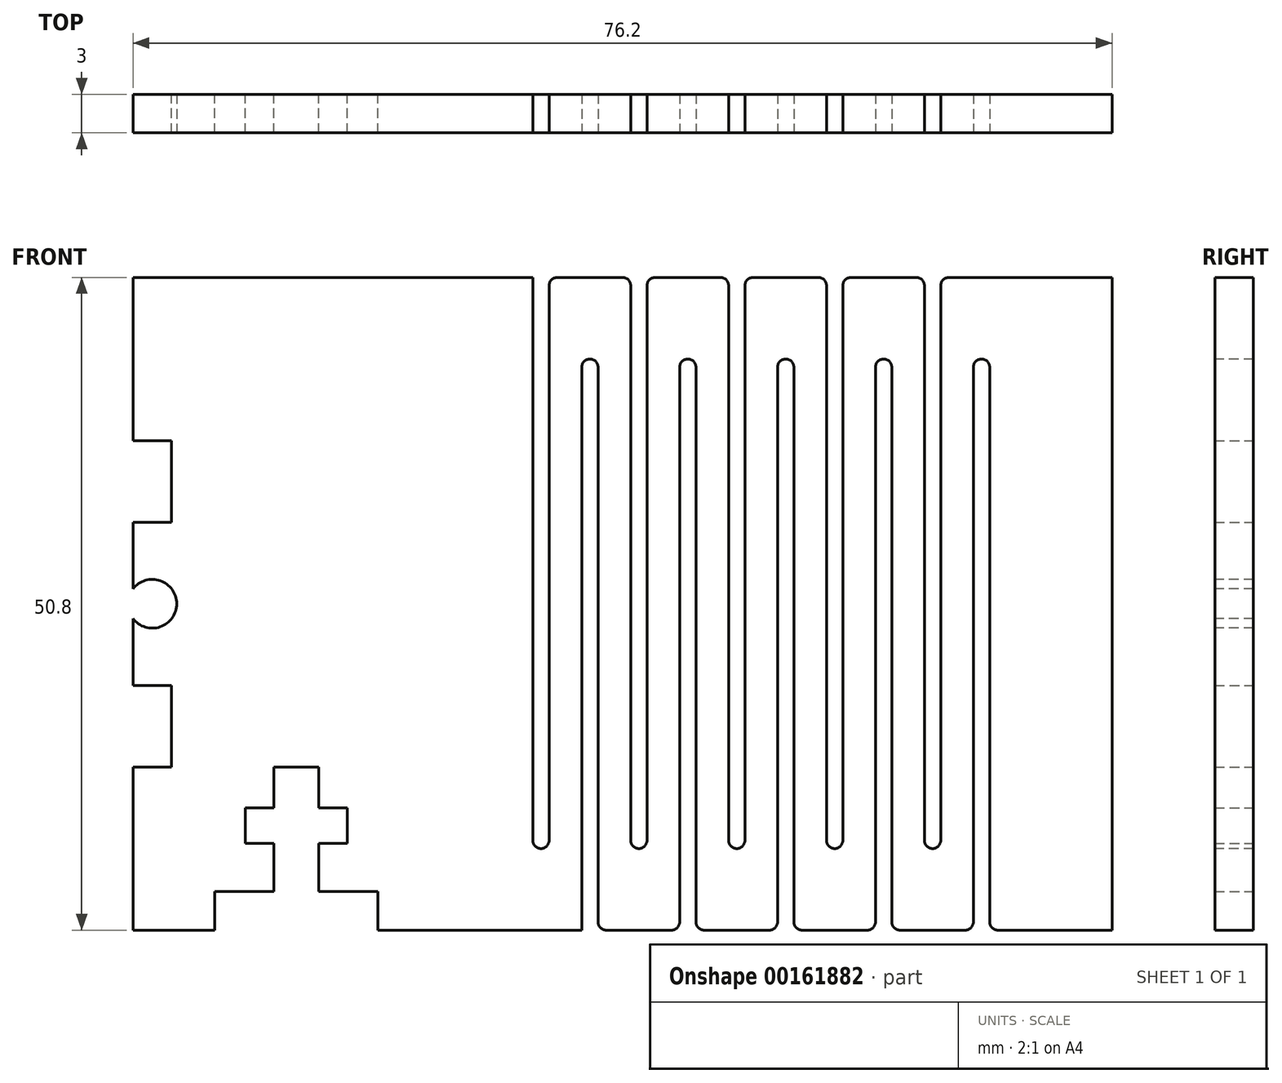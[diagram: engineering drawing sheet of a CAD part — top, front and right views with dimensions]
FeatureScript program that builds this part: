
annotation { "Feature Type Name" : "Feature", "Feature Type Description" : "" }
export const myFeature = defineFeature(function(context is Context, id is Id, definition is map)
    precondition{}
    {
        {
            var Q0;
            Q0=qCreatedBy(makeId("Front.planeOp"),FACE);
            var sketch = newSketch(context, id + "F0", { "sketchPlane" : qUnion([Q0])});
            skLineSegment(sketch, "E0.bottom", {"start": v(-38.1, 25.4) * mm, "end": v(38.1, 25.4) * mm});
            skLineSegment(sketch, "E0.top", {"start": v(-38.1, -25.4) * mm, "end": v(-31.75, -25.4) * mm});
            skLineSegment(sketch, "E0.left", {"start": v(-38.1, 25.4) * mm, "end": v(-38.1, 12.7) * mm});
            skLineSegment(sketch, "E0.right", {"start": v(38.1, 25.4) * mm, "end": v(38.1, -25.4) * mm});
            skPoint(sketch, "E0.middle", {"position": v(0, 0) * mm});
            skLineSegment(sketch, "E1", {"start": v(-31.75, -25.4) * mm, "end": v(-31.75, -22.4) * mm});
            skLineSegment(sketch, "E2", {"start": v(-31.75, -22.4) * mm, "end": v(-27.15, -22.4) * mm});
            skLineSegment(sketch, "E3", {"start": v(-23.65, -22.4) * mm, "end": v(-23.65, -18.64) * mm});
            skLineSegment(sketch, "E4", {"start": v(-29.36, -18.64) * mm, "end": v(-29.36, -15.88) * mm});
            skLineSegment(sketch, "E5", {"start": v(-23.65, -15.88) * mm, "end": v(-23.65, -12.7) * mm});
            skLineSegment(sketch, "E6", {"start": v(-27.15, -12.7) * mm, "end": v(-23.65, -12.7) * mm});
            skLineSegment(sketch, "E7", {"start": v(-27.15, -12.7) * mm, "end": v(-27.15, -15.88) * mm});
            skLineSegment(sketch, "E8", {"start": v(-27.15, -18.64) * mm, "end": v(-27.15, -22.4) * mm});
            skLineSegment(sketch, "E9", {"start": v(-19.05, -22.4) * mm, "end": v(-19.05, -25.4) * mm});
            skLineSegment(sketch, "E10", {"start": v(-25.4, -12.7) * mm, "end": v(-25.4, -25.4) * mm, "construction": true});
            skLineSegment(sketch, "E11", {"start": v(-29.36, -15.88) * mm, "end": v(-27.15, -15.88) * mm});
            skLineSegment(sketch, "E12", {"start": v(-29.36, -18.64) * mm, "end": v(-27.15, -18.64) * mm});
            skLineSegment(sketch, "E13", {"start": v(-23.65, -15.88) * mm, "end": v(-21.44, -15.88) * mm});
            skLineSegment(sketch, "E14", {"start": v(-21.44, -15.88) * mm, "end": v(-21.44, -18.64) * mm});
            skLineSegment(sketch, "E15", {"start": v(-21.44, -18.64) * mm, "end": v(-23.65, -18.64) * mm});
            skLineSegment(sketch, "E16.trimOffspring", {"start": v(-23.65, -22.4) * mm, "end": v(-19.05, -22.4) * mm});
            skLineSegment(sketch, "E17.trimOffspring", {"start": v(-19.05, -25.4) * mm, "end": v(38.1, -25.4) * mm});
            skLineSegment(sketch, "E18", {"start": v(-38.1, 6.35) * mm, "end": v(-35.1, 6.35) * mm});
            skLineSegment(sketch, "E19", {"start": v(-35.1, 6.35) * mm, "end": v(-35.1, 12.7) * mm});
            skLineSegment(sketch, "E20", {"start": v(-35.1, 12.7) * mm, "end": v(-38.1, 12.7) * mm});
            skLineSegment(sketch, "E21", {"start": v(-38.1, -6.35) * mm, "end": v(-35.1, -6.35) * mm});
            skLineSegment(sketch, "E22", {"start": v(-35.1, -6.35) * mm, "end": v(-35.1, -12.7) * mm});
            skLineSegment(sketch, "E23", {"start": v(-35.1, -12.7) * mm, "end": v(-38.1, -12.7) * mm});
            skLineSegment(sketch, "E24.trimOffspring", {"start": v(-38.1, 6.35) * mm, "end": v(-38.1, -6.35) * mm});
            skLineSegment(sketch, "E25.trimOffspring", {"start": v(-38.1, -12.7) * mm, "end": v(-38.1, -25.4) * mm});
            skSolve(sketch);
        }
        {
            var Q0;
            Q0 = qSketchRegion(id + "F0", true);
            extrude(context, id + "F1", {"entities" : qUnion([Q0]), "depth" : 3 * mm});
        }
        {
            var Q0;
            Q0=makeQuery(id+"F1.opExtrude","CAP_FACE",FACE,{"disambiguationData":[OSD([sQuery(id+"F0.wireOp",EDGE,"E0.bottom"),sQuery(id+"F0.wireOp",EDGE,"E0.top"),sQuery(id+"F0.wireOp",EDGE,"E0.left"),sQuery(id+"F0.wireOp",EDGE,"E0.right"),sQuery(id+"F0.wireOp",EDGE,"E1"),sQuery(id+"F0.wireOp",EDGE,"E2"),sQuery(id+"F0.wireOp",EDGE,"E3"),sQuery(id+"F0.wireOp",EDGE,"E4"),sQuery(id+"F0.wireOp",EDGE,"E5"),sQuery(id+"F0.wireOp",EDGE,"E6"),sQuery(id+"F0.wireOp",EDGE,"E7"),sQuery(id+"F0.wireOp",EDGE,"E8"),sQuery(id+"F0.wireOp",EDGE,"E9"),sQuery(id+"F0.wireOp",EDGE,"E11"),sQuery(id+"F0.wireOp",EDGE,"E12"),sQuery(id+"F0.wireOp",EDGE,"E13"),sQuery(id+"F0.wireOp",EDGE,"E14"),sQuery(id+"F0.wireOp",EDGE,"E15"),sQuery(id+"F0.wireOp",EDGE,"E16.trimOffspring"),sQuery(id+"F0.wireOp",EDGE,"E17.trimOffspring")])],"isStart":false});
            var sketch = newSketch(context, id + "F2", { "sketchPlane" : qUnion([Q0])});
            skLineSegment(sketch, "E26.0", {"start": v(-36.6, 6.35) * mm, "end": v(-36.6, -6.35) * mm, "construction": true});
            skPoint(sketch, "E27", {"position": v(-36.6, 0) * mm});
            skSolve(sketch);
        }
        {
            var Q0;
            Q0=sQuery(id+"F2.wireOp",VERTEX,"E27");
            var Q1;
            Q1=makeQuery(id+"F1.opExtrude","SWEPT_BODY",BODY,{"disambiguationData":[OSD([sQuery(id+"F0.wireOp",EDGE,"E0.bottom"),sQuery(id+"F0.wireOp",EDGE,"E0.top"),sQuery(id+"F0.wireOp",EDGE,"E0.left"),sQuery(id+"F0.wireOp",EDGE,"E0.right"),sQuery(id+"F0.wireOp",EDGE,"E1"),sQuery(id+"F0.wireOp",EDGE,"E2"),sQuery(id+"F0.wireOp",EDGE,"E3"),sQuery(id+"F0.wireOp",EDGE,"E4"),sQuery(id+"F0.wireOp",EDGE,"E5"),sQuery(id+"F0.wireOp",EDGE,"E6"),sQuery(id+"F0.wireOp",EDGE,"E7"),sQuery(id+"F0.wireOp",EDGE,"E8"),sQuery(id+"F0.wireOp",EDGE,"E9"),sQuery(id+"F0.wireOp",EDGE,"E11"),sQuery(id+"F0.wireOp",EDGE,"E12"),sQuery(id+"F0.wireOp",EDGE,"E13"),sQuery(id+"F0.wireOp",EDGE,"E14"),sQuery(id+"F0.wireOp",EDGE,"E15"),sQuery(id+"F0.wireOp",EDGE,"E16.trimOffspring"),sQuery(id+"F0.wireOp",EDGE,"E17.trimOffspring"),sQuery(id+"F0.wireOp",EDGE,"E18"),sQuery(id+"F0.wireOp",EDGE,"E19"),sQuery(id+"F0.wireOp",EDGE,"E20"),sQuery(id+"F0.wireOp",EDGE,"E21"),sQuery(id+"F0.wireOp",EDGE,"E22"),sQuery(id+"F0.wireOp",EDGE,"E23"),sQuery(id+"F0.wireOp",EDGE,"E24.trimOffspring"),sQuery(id+"F0.wireOp",EDGE,"E25.trimOffspring")])]});
            hole(context, id + "F3", {"style" : HoleStyle.SIMPLE, "endStyle" : HoleEndStyle.THROUGH, "standardTappedOrClearance" : lookupTablePath({ "standard" : "ANSI", "fit" : "Normal (ASME)", "size" : "#6", "type" : "Clearance" }), "standardBlindInLast" : lookupTablePath({ "fit" : "Free", "standard" : "ANSI", "size" : "#6", "type" : "Clearance" }), "holeDiameter" : 3.8 * mm, "locations" : qUnion([Q0]), "scope" : qUnion([Q1]), "isTappedThrough" : true});
        }
        {
            var Q0;
            Q0=makeQuery(id+"F1.opExtrude","CAP_FACE",FACE,{"disambiguationData":[OSD([sQuery(id+"F0.wireOp",EDGE,"E0.bottom"),sQuery(id+"F0.wireOp",EDGE,"E0.top"),sQuery(id+"F0.wireOp",EDGE,"E0.left"),sQuery(id+"F0.wireOp",EDGE,"E0.right"),sQuery(id+"F0.wireOp",EDGE,"E1"),sQuery(id+"F0.wireOp",EDGE,"E2"),sQuery(id+"F0.wireOp",EDGE,"E3"),sQuery(id+"F0.wireOp",EDGE,"E4"),sQuery(id+"F0.wireOp",EDGE,"E5"),sQuery(id+"F0.wireOp",EDGE,"E6"),sQuery(id+"F0.wireOp",EDGE,"E7"),sQuery(id+"F0.wireOp",EDGE,"E8"),sQuery(id+"F0.wireOp",EDGE,"E9"),sQuery(id+"F0.wireOp",EDGE,"E11"),sQuery(id+"F0.wireOp",EDGE,"E12"),sQuery(id+"F0.wireOp",EDGE,"E13"),sQuery(id+"F0.wireOp",EDGE,"E14"),sQuery(id+"F0.wireOp",EDGE,"E15"),sQuery(id+"F0.wireOp",EDGE,"E16.trimOffspring"),sQuery(id+"F0.wireOp",EDGE,"E17.trimOffspring"),sQuery(id+"F0.wireOp",EDGE,"E18"),sQuery(id+"F0.wireOp",EDGE,"E19"),sQuery(id+"F0.wireOp",EDGE,"E20"),sQuery(id+"F0.wireOp",EDGE,"E21"),sQuery(id+"F0.wireOp",EDGE,"E22"),sQuery(id+"F0.wireOp",EDGE,"E23"),sQuery(id+"F0.wireOp",EDGE,"E24.trimOffspring"),sQuery(id+"F0.wireOp",EDGE,"E25.trimOffspring")])],"isStart":false});
            var sketch = newSketch(context, id + "F4", { "sketchPlane" : qUnion([Q0])});
            skLineSegment(sketch, "E28", {"start": v(-12.7, 25.4) * mm, "end": v(-12.7, -25.4) * mm, "construction": true});
            skLineSegment(sketch, "E29.0", {"start": v(-6.35, 25.4) * mm, "end": v(-6.35, -19.05) * mm, "construction": true});
            skLineSegment(sketch, "E30.0", {"start": v(-6.98, 25.4) * mm, "end": v(-6.98, -19.05) * mm});
            skLineSegment(sketch, "E31.0", {"start": v(-5.71, 25.4) * mm, "end": v(-5.71, -19.05) * mm});
            skLineSegment(sketch, "E32.1.0.0", {"start": v(-3.17, 19.05) * mm, "end": v(-3.17, -25.4) * mm});
            skLineSegment(sketch, "E32.1.0.1", {"start": v(-2.54, 19.05) * mm, "end": v(-2.54, -25.4) * mm, "construction": true});
            skLineSegment(sketch, "E32.1.0.2", {"start": v(-1.9, 19.05) * mm, "end": v(-1.9, -25.4) * mm});
            skLineSegment(sketch, "E33.0", {"start": v(-3.17, 19.05) * mm, "end": v(-1.9, 19.05) * mm});
            skLineSegment(sketch, "E34.trimOffspring", {"start": v(-6.98, -19.05) * mm, "end": v(-5.71, -19.05) * mm});
            skLineSegment(sketch, "E35", {"start": v(-3.17, -25.4) * mm, "end": v(-1.9, -25.4) * mm});
            skLineSegment(sketch, "E36", {"start": v(-5.71, 25.4) * mm, "end": v(-6.98, 25.4) * mm});
            skLineSegment(sketch, "E37.1.0.0", {"start": v(5.72, 19.05) * mm, "end": v(5.72, -25.4) * mm});
            skLineSegment(sketch, "E37.1.0.1", {"start": v(1.27, 25.4) * mm, "end": v(1.27, -19.05) * mm, "construction": true});
            skLineSegment(sketch, "E37.1.0.2", {"start": v(4.45, 19.05) * mm, "end": v(4.45, -25.4) * mm});
            skLineSegment(sketch, "E37.1.0.3", {"start": v(0.64, 25.4) * mm, "end": v(0.64, -19.05) * mm});
            skLineSegment(sketch, "E37.1.0.4", {"start": v(1.9, 25.4) * mm, "end": v(1.9, -19.05) * mm});
            skLineSegment(sketch, "E37.1.0.5", {"start": v(5.08, 19.05) * mm, "end": v(5.08, -25.4) * mm, "construction": true});
            skLineSegment(sketch, "E37.1.0.6", {"start": v(0.64, -19.05) * mm, "end": v(1.9, -19.05) * mm});
            skLineSegment(sketch, "E37.1.0.7", {"start": v(4.45, -25.4) * mm, "end": v(5.72, -25.4) * mm});
            skLineSegment(sketch, "E37.1.0.8", {"start": v(1.9, 25.4) * mm, "end": v(0.64, 25.4) * mm});
            skLineSegment(sketch, "E37.1.0.9", {"start": v(4.45, 19.05) * mm, "end": v(5.72, 19.05) * mm});
            skLineSegment(sketch, "E37.2.0.0", {"start": v(13.34, 19.05) * mm, "end": v(13.34, -25.4) * mm});
            skLineSegment(sketch, "E37.2.0.1", {"start": v(8.9, 25.4) * mm, "end": v(8.9, -19.05) * mm, "construction": true});
            skLineSegment(sketch, "E37.2.0.2", {"start": v(12.07, 19.05) * mm, "end": v(12.07, -25.4) * mm});
            skLineSegment(sketch, "E37.2.0.3", {"start": v(8.26, 25.4) * mm, "end": v(8.26, -19.05) * mm});
            skLineSegment(sketch, "E37.2.0.4", {"start": v(9.53, 25.4) * mm, "end": v(9.53, -19.05) * mm});
            skLineSegment(sketch, "E37.2.0.5", {"start": v(12.7, 19.05) * mm, "end": v(12.7, -25.4) * mm, "construction": true});
            skLineSegment(sketch, "E37.2.0.6", {"start": v(8.26, -19.05) * mm, "end": v(9.53, -19.05) * mm});
            skLineSegment(sketch, "E37.2.0.7", {"start": v(12.07, -25.4) * mm, "end": v(13.34, -25.4) * mm});
            skLineSegment(sketch, "E37.2.0.8", {"start": v(9.53, 25.4) * mm, "end": v(8.26, 25.4) * mm});
            skLineSegment(sketch, "E37.2.0.9", {"start": v(12.07, 19.05) * mm, "end": v(13.34, 19.05) * mm});
            skLineSegment(sketch, "E37.3.0.0", {"start": v(20.96, 19.05) * mm, "end": v(20.96, -25.4) * mm});
            skLineSegment(sketch, "E37.3.0.1", {"start": v(16.51, 25.4) * mm, "end": v(16.51, -19.05) * mm, "construction": true});
            skLineSegment(sketch, "E37.3.0.2", {"start": v(19.69, 19.05) * mm, "end": v(19.69, -25.4) * mm});
            skLineSegment(sketch, "E37.3.0.3", {"start": v(15.88, 25.4) * mm, "end": v(15.88, -19.05) * mm});
            skLineSegment(sketch, "E37.3.0.4", {"start": v(17.15, 25.4) * mm, "end": v(17.15, -19.05) * mm});
            skLineSegment(sketch, "E37.3.0.5", {"start": v(20.32, 19.05) * mm, "end": v(20.32, -25.4) * mm, "construction": true});
            skLineSegment(sketch, "E37.3.0.6", {"start": v(15.88, -19.05) * mm, "end": v(17.15, -19.05) * mm});
            skLineSegment(sketch, "E37.3.0.7", {"start": v(19.69, -25.4) * mm, "end": v(20.96, -25.4) * mm});
            skLineSegment(sketch, "E37.3.0.8", {"start": v(17.15, 25.4) * mm, "end": v(15.88, 25.4) * mm});
            skLineSegment(sketch, "E37.3.0.9", {"start": v(19.69, 19.05) * mm, "end": v(20.96, 19.05) * mm});
            skLineSegment(sketch, "E37.4.0.0", {"start": v(28.58, 19.05) * mm, "end": v(28.58, -25.4) * mm});
            skLineSegment(sketch, "E37.4.0.1", {"start": v(24.13, 25.4) * mm, "end": v(24.13, -19.05) * mm, "construction": true});
            skLineSegment(sketch, "E37.4.0.2", {"start": v(27.3, 19.05) * mm, "end": v(27.3, -25.4) * mm});
            skLineSegment(sketch, "E37.4.0.3", {"start": v(23.5, 25.4) * mm, "end": v(23.5, -19.05) * mm});
            skLineSegment(sketch, "E37.4.0.4", {"start": v(24.77, 25.4) * mm, "end": v(24.77, -19.05) * mm});
            skLineSegment(sketch, "E37.4.0.5", {"start": v(27.94, 19.05) * mm, "end": v(27.94, -25.4) * mm, "construction": true});
            skLineSegment(sketch, "E37.4.0.6", {"start": v(23.5, -19.05) * mm, "end": v(24.77, -19.05) * mm});
            skLineSegment(sketch, "E37.4.0.7", {"start": v(27.3, -25.4) * mm, "end": v(28.58, -25.4) * mm});
            skLineSegment(sketch, "E37.4.0.8", {"start": v(24.77, 25.4) * mm, "end": v(23.5, 25.4) * mm});
            skLineSegment(sketch, "E37.4.0.9", {"start": v(27.3, 19.05) * mm, "end": v(28.58, 19.05) * mm});
            skLineSegment(sketch, "E37.direction1", {"start": v(-3.17, -25.4) * mm, "end": v(4.45, -25.4) * mm, "construction": true});
            skSolve(sketch);
        }
        {
            var Q0;
            Q0 = qSketchRegion(id + "F4", true);
            extrude(context, id + "F5", {"entities" : qUnion([Q0]), "operationType" : NewBodyOperationType.REMOVE, "endBound" : BoundingType.THROUGH_ALL, "oppositeDirection" : true, "depth" : 25.4 * mm});
        }
        {
            var Q0;
            Q0=makeQuery(id+"F5.boolean.opBoolean","COPY",EDGE,{"derivedFrom":makeQuery(id+"F5.opExtrude","SWEPT_EDGE",EDGE,{"disambiguationData":[OSD([sQuery(id+"F4.wireOp",EDGE,"E30.0"),sQuery(id+"F4.wireOp",EDGE,"E34.trimOffspring")])]})});
            var Q1;
            Q1=makeQuery(id+"F5.boolean.opBoolean","COPY",EDGE,{"derivedFrom":makeQuery(id+"F5.opExtrude","SWEPT_EDGE",EDGE,{"disambiguationData":[OSD([sQuery(id+"F4.wireOp",EDGE,"E31.0"),sQuery(id+"F4.wireOp",EDGE,"E34.trimOffspring")])]})});
            var Q2;
            Q2=makeQuery(id+"F5.boolean.opBoolean","COPY",EDGE,{"derivedFrom":makeQuery(id+"F5.opExtrude","SWEPT_EDGE",EDGE,{"disambiguationData":[OSD([sQuery(id+"F4.wireOp",EDGE,"E37.1.0.3"),sQuery(id+"F4.wireOp",EDGE,"E37.1.0.6")])]})});
            var Q3;
            Q3=makeQuery(id+"F5.boolean.opBoolean","COPY",EDGE,{"derivedFrom":makeQuery(id+"F5.opExtrude","SWEPT_EDGE",EDGE,{"disambiguationData":[OSD([sQuery(id+"F4.wireOp",EDGE,"E37.1.0.4"),sQuery(id+"F4.wireOp",EDGE,"E37.1.0.6")])]})});
            var Q4;
            Q4=makeQuery(id+"F5.boolean.opBoolean","COPY",EDGE,{"derivedFrom":makeQuery(id+"F5.opExtrude","SWEPT_EDGE",EDGE,{"disambiguationData":[OSD([sQuery(id+"F4.wireOp",EDGE,"E37.2.0.4"),sQuery(id+"F4.wireOp",EDGE,"E37.2.0.6")])]})});
            var Q5;
            Q5=makeQuery(id+"F5.boolean.opBoolean","COPY",EDGE,{"derivedFrom":makeQuery(id+"F5.opExtrude","SWEPT_EDGE",EDGE,{"disambiguationData":[OSD([sQuery(id+"F4.wireOp",EDGE,"E37.2.0.3"),sQuery(id+"F4.wireOp",EDGE,"E37.2.0.6")])]})});
            var Q6;
            Q6=makeQuery(id+"F5.boolean.opBoolean","COPY",EDGE,{"derivedFrom":makeQuery(id+"F5.opExtrude","SWEPT_EDGE",EDGE,{"disambiguationData":[OSD([sQuery(id+"F4.wireOp",EDGE,"E37.3.0.3"),sQuery(id+"F4.wireOp",EDGE,"E37.3.0.6")])]})});
            var Q7;
            Q7=makeQuery(id+"F5.boolean.opBoolean","COPY",EDGE,{"derivedFrom":makeQuery(id+"F5.opExtrude","SWEPT_EDGE",EDGE,{"disambiguationData":[OSD([sQuery(id+"F4.wireOp",EDGE,"E37.3.0.4"),sQuery(id+"F4.wireOp",EDGE,"E37.3.0.6")])]})});
            var Q8;
            Q8=makeQuery(id+"F5.boolean.opBoolean","COPY",EDGE,{"derivedFrom":makeQuery(id+"F5.opExtrude","SWEPT_EDGE",EDGE,{"disambiguationData":[OSD([sQuery(id+"F4.wireOp",EDGE,"E37.4.0.4"),sQuery(id+"F4.wireOp",EDGE,"E37.4.0.6")])]})});
            var Q9;
            Q9=makeQuery(id+"F5.boolean.opBoolean","COPY",EDGE,{"derivedFrom":makeQuery(id+"F5.opExtrude","SWEPT_EDGE",EDGE,{"disambiguationData":[OSD([sQuery(id+"F4.wireOp",EDGE,"E37.4.0.3"),sQuery(id+"F4.wireOp",EDGE,"E37.4.0.6")])]})});
            var Q10;
            Q10=makeQuery(id+"F5.boolean.opBoolean","COPY",EDGE,{"derivedFrom":makeQuery(id+"F5.opExtrude","SWEPT_EDGE",EDGE,{"disambiguationData":[OSD([sQuery(id+"F4.wireOp",EDGE,"E32.1.0.0"),sQuery(id+"F4.wireOp",EDGE,"E33.0")])]})});
            var Q11;
            Q11=makeQuery(id+"F5.boolean.opBoolean","COPY",EDGE,{"derivedFrom":makeQuery(id+"F5.opExtrude","SWEPT_EDGE",EDGE,{"disambiguationData":[OSD([sQuery(id+"F4.wireOp",EDGE,"E37.1.0.2"),sQuery(id+"F4.wireOp",EDGE,"E37.1.0.9")])]})});
            var Q12;
            Q12=makeQuery(id+"F5.boolean.opBoolean","COPY",EDGE,{"derivedFrom":makeQuery(id+"F5.opExtrude","SWEPT_EDGE",EDGE,{"disambiguationData":[OSD([sQuery(id+"F4.wireOp",EDGE,"E37.2.0.2"),sQuery(id+"F4.wireOp",EDGE,"E37.2.0.9")])]})});
            var Q13;
            Q13=makeQuery(id+"F5.boolean.opBoolean","COPY",EDGE,{"derivedFrom":makeQuery(id+"F5.opExtrude","SWEPT_EDGE",EDGE,{"disambiguationData":[OSD([sQuery(id+"F4.wireOp",EDGE,"E37.3.0.2"),sQuery(id+"F4.wireOp",EDGE,"E37.3.0.9")])]})});
            var Q14;
            Q14=makeQuery(id+"F5.boolean.opBoolean","COPY",EDGE,{"derivedFrom":makeQuery(id+"F5.opExtrude","SWEPT_EDGE",EDGE,{"disambiguationData":[OSD([sQuery(id+"F4.wireOp",EDGE,"E37.4.0.2"),sQuery(id+"F4.wireOp",EDGE,"E37.4.0.9")])]})});
            var Q15;
            Q15=makeQuery(id+"F5.boolean.opBoolean","COPY",EDGE,{"derivedFrom":makeQuery(id+"F5.opExtrude","SWEPT_EDGE",EDGE,{"disambiguationData":[OSD([sQuery(id+"F4.wireOp",EDGE,"E32.1.0.2"),sQuery(id+"F4.wireOp",EDGE,"E33.0")])]})});
            var Q16;
            Q16=makeQuery(id+"F5.boolean.opBoolean","COPY",EDGE,{"derivedFrom":makeQuery(id+"F5.opExtrude","SWEPT_EDGE",EDGE,{"disambiguationData":[OSD([sQuery(id+"F4.wireOp",EDGE,"E37.1.0.0"),sQuery(id+"F4.wireOp",EDGE,"E37.1.0.9")])]})});
            var Q17;
            Q17=makeQuery(id+"F5.boolean.opBoolean","COPY",EDGE,{"derivedFrom":makeQuery(id+"F5.opExtrude","SWEPT_EDGE",EDGE,{"disambiguationData":[OSD([sQuery(id+"F4.wireOp",EDGE,"E37.2.0.0"),sQuery(id+"F4.wireOp",EDGE,"E37.2.0.9")])]})});
            var Q18;
            Q18=makeQuery(id+"F5.boolean.opBoolean","COPY",EDGE,{"derivedFrom":makeQuery(id+"F5.opExtrude","SWEPT_EDGE",EDGE,{"disambiguationData":[OSD([sQuery(id+"F4.wireOp",EDGE,"E37.3.0.0"),sQuery(id+"F4.wireOp",EDGE,"E37.3.0.9")])]})});
            var Q19;
            Q19=makeQuery(id+"F5.boolean.opBoolean","COPY",EDGE,{"derivedFrom":makeQuery(id+"F5.opExtrude","SWEPT_EDGE",EDGE,{"disambiguationData":[OSD([sQuery(id+"F4.wireOp",EDGE,"E37.4.0.0"),sQuery(id+"F4.wireOp",EDGE,"E37.4.0.9")])]})});
            var Q20;
            Q20=makeQuery(id+"F5.boolean.opBoolean","COPY",EDGE,{"derivedFrom":makeQuery(id+"F5.opExtrude","SWEPT_EDGE",EDGE,{"disambiguationData":[OSD([sQuery(id+"F0.wireOp",EDGE,"E17.trimOffspring"),sQuery(id+"F4.wireOp",EDGE,"E32.1.0.2"),sQuery(id+"F4.wireOp",EDGE,"E35")])]})});
            var Q21;
            Q21=makeQuery(id+"F5.boolean.opBoolean","COPY",EDGE,{"derivedFrom":makeQuery(id+"F5.opExtrude","SWEPT_EDGE",EDGE,{"disambiguationData":[OSD([sQuery(id+"F0.wireOp",EDGE,"E17.trimOffspring"),sQuery(id+"F4.wireOp",EDGE,"E37.1.0.2"),sQuery(id+"F4.wireOp",EDGE,"E37.1.0.7")])]})});
            var Q22;
            Q22=makeQuery(id+"F5.boolean.opBoolean","COPY",EDGE,{"derivedFrom":makeQuery(id+"F5.opExtrude","SWEPT_EDGE",EDGE,{"disambiguationData":[OSD([sQuery(id+"F0.wireOp",EDGE,"E17.trimOffspring"),sQuery(id+"F4.wireOp",EDGE,"E37.1.0.0"),sQuery(id+"F4.wireOp",EDGE,"E37.1.0.7")])]})});
            var Q23;
            Q23=makeQuery(id+"F5.boolean.opBoolean","COPY",EDGE,{"derivedFrom":makeQuery(id+"F5.opExtrude","SWEPT_EDGE",EDGE,{"disambiguationData":[OSD([sQuery(id+"F0.wireOp",EDGE,"E17.trimOffspring"),sQuery(id+"F4.wireOp",EDGE,"E37.2.0.2"),sQuery(id+"F4.wireOp",EDGE,"E37.2.0.7")])]})});
            var Q24;
            Q24=makeQuery(id+"F5.boolean.opBoolean","COPY",EDGE,{"derivedFrom":makeQuery(id+"F5.opExtrude","SWEPT_EDGE",EDGE,{"disambiguationData":[OSD([sQuery(id+"F0.wireOp",EDGE,"E17.trimOffspring"),sQuery(id+"F4.wireOp",EDGE,"E37.2.0.0"),sQuery(id+"F4.wireOp",EDGE,"E37.2.0.7")])]})});
            var Q25;
            Q25=makeQuery(id+"F5.boolean.opBoolean","COPY",EDGE,{"derivedFrom":makeQuery(id+"F5.opExtrude","SWEPT_EDGE",EDGE,{"disambiguationData":[OSD([sQuery(id+"F0.wireOp",EDGE,"E17.trimOffspring"),sQuery(id+"F4.wireOp",EDGE,"E37.3.0.2"),sQuery(id+"F4.wireOp",EDGE,"E37.3.0.7")])]})});
            var Q26;
            Q26=makeQuery(id+"F5.boolean.opBoolean","COPY",EDGE,{"derivedFrom":makeQuery(id+"F5.opExtrude","SWEPT_EDGE",EDGE,{"disambiguationData":[OSD([sQuery(id+"F0.wireOp",EDGE,"E17.trimOffspring"),sQuery(id+"F4.wireOp",EDGE,"E37.3.0.0"),sQuery(id+"F4.wireOp",EDGE,"E37.3.0.7")])]})});
            var Q27;
            Q27=makeQuery(id+"F5.boolean.opBoolean","COPY",EDGE,{"derivedFrom":makeQuery(id+"F5.opExtrude","SWEPT_EDGE",EDGE,{"disambiguationData":[OSD([sQuery(id+"F0.wireOp",EDGE,"E17.trimOffspring"),sQuery(id+"F4.wireOp",EDGE,"E37.4.0.2"),sQuery(id+"F4.wireOp",EDGE,"E37.4.0.7")])]})});
            var Q28;
            Q28=makeQuery(id+"F5.boolean.opBoolean","COPY",EDGE,{"derivedFrom":makeQuery(id+"F5.opExtrude","SWEPT_EDGE",EDGE,{"disambiguationData":[OSD([sQuery(id+"F0.wireOp",EDGE,"E17.trimOffspring"),sQuery(id+"F4.wireOp",EDGE,"E37.4.0.0"),sQuery(id+"F4.wireOp",EDGE,"E37.4.0.7")])]})});
            var Q29;
            Q29=makeQuery(id+"F5.boolean.opBoolean","COPY",EDGE,{"derivedFrom":makeQuery(id+"F5.opExtrude","SWEPT_EDGE",EDGE,{"disambiguationData":[OSD([sQuery(id+"F0.wireOp",EDGE,"E0.bottom"),sQuery(id+"F4.wireOp",EDGE,"E30.0"),sQuery(id+"F4.wireOp",EDGE,"E36")])]})});
            var Q30;
            Q30=makeQuery(id+"F5.boolean.opBoolean","COPY",EDGE,{"derivedFrom":makeQuery(id+"F5.opExtrude","SWEPT_EDGE",EDGE,{"disambiguationData":[OSD([sQuery(id+"F0.wireOp",EDGE,"E0.bottom"),sQuery(id+"F4.wireOp",EDGE,"E31.0"),sQuery(id+"F4.wireOp",EDGE,"E36")])]})});
            var Q31;
            Q31=makeQuery(id+"F5.boolean.opBoolean","COPY",EDGE,{"derivedFrom":makeQuery(id+"F5.opExtrude","SWEPT_EDGE",EDGE,{"disambiguationData":[OSD([sQuery(id+"F0.wireOp",EDGE,"E17.trimOffspring"),sQuery(id+"F4.wireOp",EDGE,"E32.1.0.0"),sQuery(id+"F4.wireOp",EDGE,"E35")])]})});
            var Q32;
            Q32=makeQuery(id+"F5.boolean.opBoolean","COPY",EDGE,{"derivedFrom":makeQuery(id+"F5.opExtrude","SWEPT_EDGE",EDGE,{"disambiguationData":[OSD([sQuery(id+"F0.wireOp",EDGE,"E0.bottom"),sQuery(id+"F4.wireOp",EDGE,"E37.1.0.3"),sQuery(id+"F4.wireOp",EDGE,"E37.1.0.8")])]})});
            var Q33;
            Q33=makeQuery(id+"F5.boolean.opBoolean","COPY",EDGE,{"derivedFrom":makeQuery(id+"F5.opExtrude","SWEPT_EDGE",EDGE,{"disambiguationData":[OSD([sQuery(id+"F0.wireOp",EDGE,"E0.bottom"),sQuery(id+"F4.wireOp",EDGE,"E37.1.0.4"),sQuery(id+"F4.wireOp",EDGE,"E37.1.0.8")])]})});
            var Q34;
            Q34=makeQuery(id+"F5.boolean.opBoolean","COPY",EDGE,{"derivedFrom":makeQuery(id+"F5.opExtrude","SWEPT_EDGE",EDGE,{"disambiguationData":[OSD([sQuery(id+"F0.wireOp",EDGE,"E0.bottom"),sQuery(id+"F4.wireOp",EDGE,"E37.2.0.3"),sQuery(id+"F4.wireOp",EDGE,"E37.2.0.8")])]})});
            var Q35;
            Q35=makeQuery(id+"F5.boolean.opBoolean","COPY",EDGE,{"derivedFrom":makeQuery(id+"F5.opExtrude","SWEPT_EDGE",EDGE,{"disambiguationData":[OSD([sQuery(id+"F0.wireOp",EDGE,"E0.bottom"),sQuery(id+"F4.wireOp",EDGE,"E37.2.0.4"),sQuery(id+"F4.wireOp",EDGE,"E37.2.0.8")])]})});
            var Q36;
            Q36=makeQuery(id+"F5.boolean.opBoolean","COPY",EDGE,{"derivedFrom":makeQuery(id+"F5.opExtrude","SWEPT_EDGE",EDGE,{"disambiguationData":[OSD([sQuery(id+"F0.wireOp",EDGE,"E0.bottom"),sQuery(id+"F4.wireOp",EDGE,"E37.3.0.3"),sQuery(id+"F4.wireOp",EDGE,"E37.3.0.8")])]})});
            var Q37;
            Q37=makeQuery(id+"F5.boolean.opBoolean","COPY",EDGE,{"derivedFrom":makeQuery(id+"F5.opExtrude","SWEPT_EDGE",EDGE,{"disambiguationData":[OSD([sQuery(id+"F0.wireOp",EDGE,"E0.bottom"),sQuery(id+"F4.wireOp",EDGE,"E37.3.0.4"),sQuery(id+"F4.wireOp",EDGE,"E37.3.0.8")])]})});
            var Q38;
            Q38=makeQuery(id+"F5.boolean.opBoolean","COPY",EDGE,{"derivedFrom":makeQuery(id+"F5.opExtrude","SWEPT_EDGE",EDGE,{"disambiguationData":[OSD([sQuery(id+"F0.wireOp",EDGE,"E0.bottom"),sQuery(id+"F4.wireOp",EDGE,"E37.4.0.3"),sQuery(id+"F4.wireOp",EDGE,"E37.4.0.8")])]})});
            var Q39;
            Q39=makeQuery(id+"F5.boolean.opBoolean","COPY",EDGE,{"derivedFrom":makeQuery(id+"F5.opExtrude","SWEPT_EDGE",EDGE,{"disambiguationData":[OSD([sQuery(id+"F0.wireOp",EDGE,"E0.bottom"),sQuery(id+"F4.wireOp",EDGE,"E37.4.0.4"),sQuery(id+"F4.wireOp",EDGE,"E37.4.0.8")])]})});
            fillet(context, id + "F6", {"entities" : qUnion([Q0, Q1, Q2, Q3, Q4, Q5, Q6, Q7, Q8, Q9, Q10, Q11, Q12, Q13, Q14, Q15, Q16, Q17, Q18, Q19, Q20, Q21, Q22, Q23, Q24, Q25, Q26, Q27, Q28, Q29, Q30, Q31, Q32, Q33, Q34, Q35, Q36, Q37, Q38, Q39]), "radius" : 0.64 * mm, "tangentPropagation" : true, "allowEdgeOverflow" : false});
        }
    });
